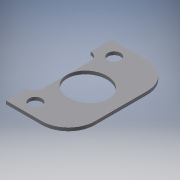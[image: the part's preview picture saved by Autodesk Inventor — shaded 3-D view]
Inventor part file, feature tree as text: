
AUTODESK INVENTOR PART (.ipt)
format: ipt  version: 2017 (Build 210142000, 142)  size: 112,640 bytes
history: native  units: mm
features: other x4, extrude x1, sketch x1, reference x1
ambient origin geometry x8: Origin, YZ Plane, XZ Plane, XY Plane, X Axis, Y Axis, Z Axis, Center Point
bodies: Body1 (feature_tree)
feature tree (7):
  other  "Bryła1"
  extrude  "Wyciągnięcie proste1"  Depth=1.0mm TaperAngle=0.0deg
  sketch  "Szkic1"
  reference  "Odniesienie1"
  other  "<userpath>\Desktop\quadrocopter rysunki\Zespół3.iam"
  other  "Zespół3.iam"
  other  "podwozie:1"
